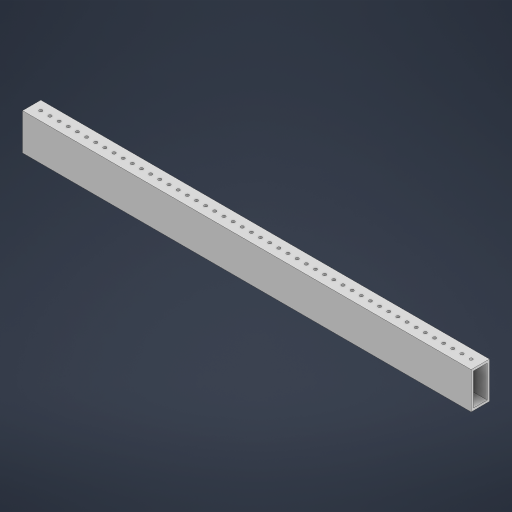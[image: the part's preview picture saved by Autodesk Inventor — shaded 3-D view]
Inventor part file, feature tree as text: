
AUTODESK INVENTOR PART (.ipt)
format: ipt  version: 2023 (Build 270158000, 158)  size: 263,680 bytes
history: native  units: in
note: dims shown in document units (in); Inventor stores cm internally (conversion verified against a paired STEP export)
features: sketch x2, extrude x1, shell x1, hole x1, pattern_linear x1
ambient origin geometry x8: Origin, YZ Plane, XZ Plane, XY Plane, X Axis, Y Axis, Z Axis, Center Point
bodies: Solid1 (feature_tree)
feature tree (6):
  extrude  "Extrusion1"  Depth=1.0in
  shell  "Shell1"  Thickness=24.5in
  hole  "Hole1"  [1 undecoded]
  pattern_linear  "Rectangular Pattern1"  Spacing1=0.5in  [1 undecoded]
  sketch  "Sketch1"  dims[d0=2.0in d1=1.0in d2=24.5in d3=0.0in]
  sketch  "Sketch2"  dims[d4=0.125in d5=0.1625in d6=0.5in d7=0.1625in d8=0.75in d9=0.375in d10=0.25in d11=0.5635in d12=1.0in d13=0.8108in d14=18.8976in d16=0.5in]
note: 2 required parameter values undecoded (feature->parameter linkage not recoverable at this tier; creation-order binding heuristic only, values carry confidence <= 0.55)
